# Revit family: Bath_Mixer-GROHE-Lineare-23792_Series
name_source: partatom
category: Plumbing Fixtures
revit_build: Autodesk Revit 2014 (Build: 20130308_1515(x64)
units: mm (PartAtom-declared; Revit-internal decimal feet)

## types (2) — shared parameters
Assembly Code = D2020300
CW Connection = Yes
CWFU = 3
Cold Water Connection Diameter = 1/2"
Default Elevation = 0"
Description = Lineare Single-Handle Bathtub Faucet
Flow Rate = 5.0 gpm (1.9 L/min), 2.4 gpm (9 L/min) for Handshower
HW Connection = Yes
HWFU = 3
Height = 31 9/16"
Hose Height = 22 5/8"
Hot Water Connection Diameter = 1"
Installation Type = Surface Mounted
Length = 10 7/8"
Manufacturer = GROHE
Price = Prices may vary. Please consult Manufacturer Representative for most up-to-date price list.
Product Page URL = https://www.grohe.us
Shipping Weight = 0.00 lb
Tempered Water Connection Diameter = 1/2"
URL = https://www.grohe.us
Vent Connection = No
WFU = 4
Warranty Information = Limited Lifetime Warranty
Waste Connection = No
Width = 6 11/16"

## per-type parameters (varying)
| type | Finish | Material |
| 23792001 | Metal-Grohe-001-Starlight Chrome | Metal-Grohe-001-Starlight Chrome |
| 23792EN1 | Metal-Grohe-EN1-Brushed Nickel | Metal-Grohe-EN1-Brushed Nickel |

note: column(s) folded — value = type name in every type: Model

## geometry (parser evidence)
native form markers: Sweep x1
no freeform markers — native parametric forms only
